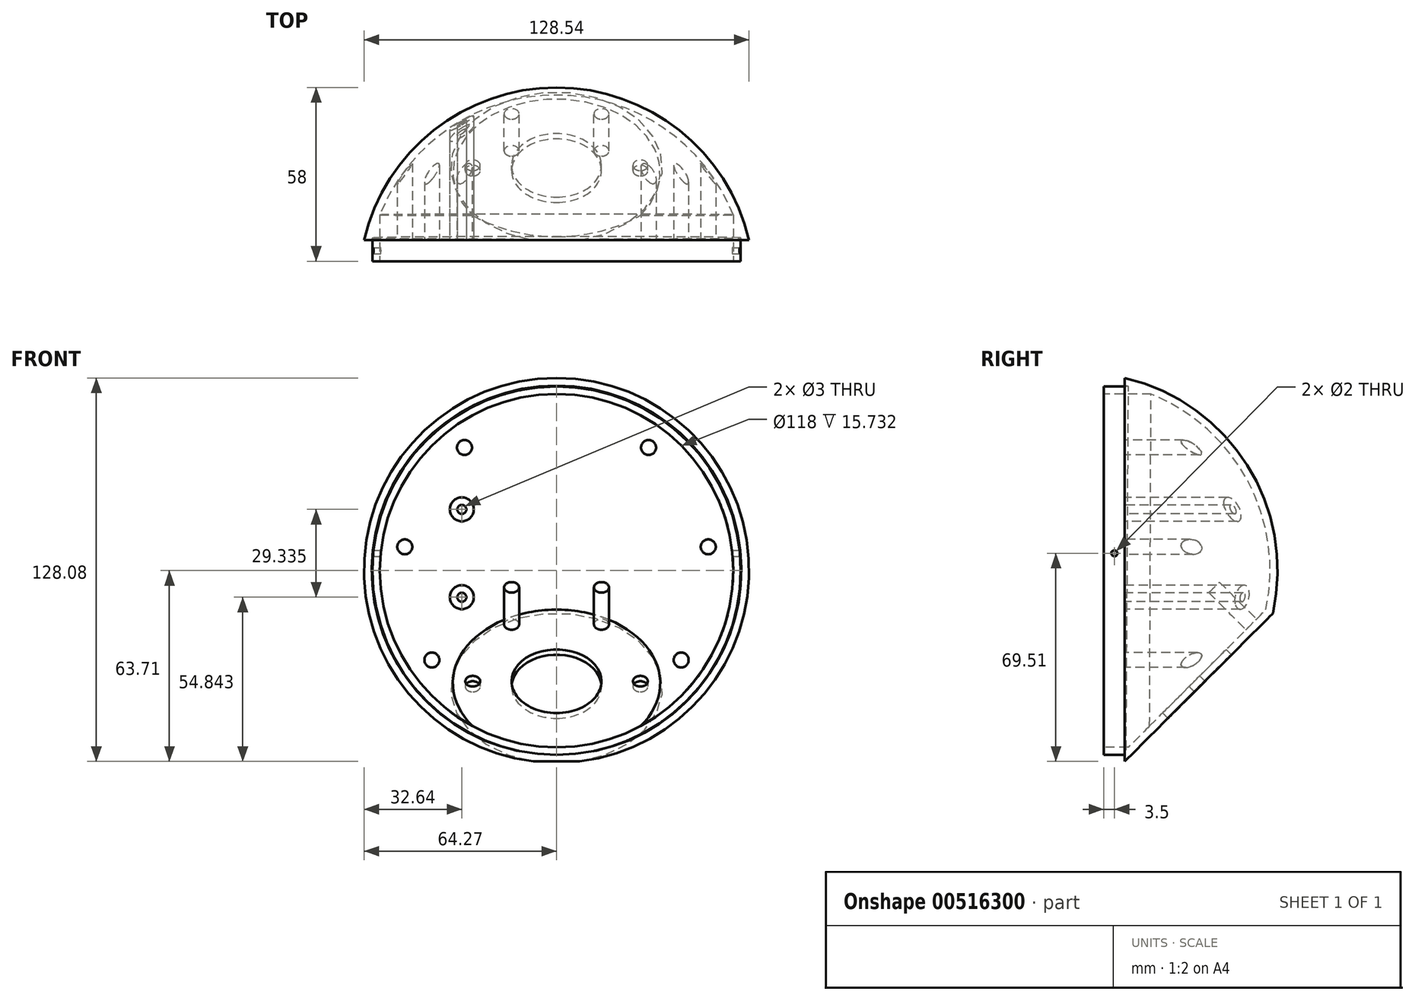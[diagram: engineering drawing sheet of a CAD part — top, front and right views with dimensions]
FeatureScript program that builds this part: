
annotation { "Feature Type Name" : "Feature", "Feature Type Description" : "" }
export const myFeature = defineFeature(function(context is Context, id is Id, definition is map)
    precondition{}
    {
        {
            var Q0;
            Q0=qCreatedBy(makeId("Front.planeOp"),FACE);
            var sketch = newSketch(context, id + "F0", { "sketchPlane" : qUnion([Q0])});
            skLineSegment(sketch, "E0", {"start": v(0, 60.3) * mm, "end": v(0, -71.7) * mm});
            skArc(sketch, "E1", {"start": v(0, 60.3) * mm, "mid": v(-66, -5.7) * mm, "end": v(0, -71.7) * mm});
            skSolve(sketch);
        }
        {
            var Q0;
            Q0=qSketchRegion(id+"F0",true);
            var Q1;
            Q1=sQuery(id+"F0.wireOp",EDGE,"E0");
            revolve(context, id + "F1", {"entities" : qUnion([Q0]), "axis" : qUnion([Q1]), "revolveType" : RevolveType.FULL});
        }
        {
            var Q0;
            Q0=qCreatedBy(makeId("Front.planeOp"),FACE);
            cPlane(context, id + "F2", {"entities" : qUnion([Q0]), "cplaneType" : CPlaneType.OFFSET, "offset" : 15 * mm, "oppositeDirection" : true, "width" : 150 * mm, "height" : 150 * mm});
        }
        {
            var Q0;
            Q0=qCreatedBy(id+"F2.planeOp",FACE);
            var sketch = newSketch(context, id + "F3", { "sketchPlane" : qUnion([Q0])});
            skLineSegment(sketch, "E2", {"start": v(74.9, -69.5) * mm, "end": v(-74.9, -69.5) * mm});
            skSolve(sketch);
        }
        {
            var Q0;
            Q0=sQuery(id+"F3.wireOp",EDGE,"E2");
            cPlane(context, id + "F4", {"entities" : qUnion([Q0]), "cplaneType" : CPlaneType.LINE_ANGLE, "offset" : 25 * mm, "angle" : 45 * degree, "width" : 150 * mm, "height" : 150 * mm});
        }
        {
            var Q0;
            Q0=qCreatedBy(id+"F4.planeOp",FACE);
            var sketch = newSketch(context, id + "F5", { "sketchPlane" : qUnion([Q0])});
            skLineSegment(sketch, "E3.bottom", {"start": v(55.31, 47.63) * mm, "end": v(-66.99, 47.63) * mm});
            skLineSegment(sketch, "E3.top", {"start": v(55.31, -55.11) * mm, "end": v(-66.99, -55.11) * mm});
            skLineSegment(sketch, "E3.left", {"start": v(55.31, 47.63) * mm, "end": v(55.31, -55.11) * mm});
            skLineSegment(sketch, "E3.right", {"start": v(-66.99, 47.63) * mm, "end": v(-66.99, -55.11) * mm});
            skSolve(sketch);
        }
        {
            var Q0;
            Q0=qSketchRegion(id+"F5",true);
            extrude(context, id + "F6", {"entities" : qUnion([Q0]), "operationType" : NewBodyOperationType.REMOVE, "oppositeDirection" : true, "depth" : 25 * mm, "offsetDistance" : 25 * mm});
        }
        {
            var Q0;
            Q0=qCreatedBy(id+"F2.planeOp",FACE);
            var sketch = newSketch(context, id + "F7", { "sketchPlane" : qUnion([Q0])});
            skLineSegment(sketch, "E4.bottom", {"start": v(74.83, 74.85) * mm, "end": v(-74.83, 74.85) * mm});
            skLineSegment(sketch, "E4.top", {"start": v(74.83, -74.85) * mm, "end": v(-74.83, -74.85) * mm});
            skLineSegment(sketch, "E4.left", {"start": v(74.83, 74.85) * mm, "end": v(74.83, -74.85) * mm});
            skLineSegment(sketch, "E4.right", {"start": v(-74.83, 74.85) * mm, "end": v(-74.83, -74.85) * mm});
            skPoint(sketch, "E4.middle", {"position": v(0, 0) * mm});
            skSolve(sketch);
        }
        {
            var Q0;
            Q0 = qSketchRegion(id + "F7", true);
            extrude(context, id + "F8", {"entities" : qUnion([Q0]), "operationType" : NewBodyOperationType.REMOVE, "depth" : 90 * mm, "offsetDistance" : 25 * mm});
        }
        {
            var Q0;
            Q0=makeQuery(id+"F8.boolean.opBoolean","COPY",FACE,{"derivedFrom":makeQuery(id+"F8.opExtrude","CAP_FACE",FACE,{"disambiguationData":[OSD([sQuery(id+"F7.wireOp",EDGE,"E4.bottom"),sQuery(id+"F7.wireOp",EDGE,"E4.top"),sQuery(id+"F7.wireOp",EDGE,"E4.left"),sQuery(id+"F7.wireOp",EDGE,"E4.right")])],"isStart":true})});
            shell(context, id + "F9", {"entities" : qUnion([Q0]), "thickness" : 2.5 * mm});
        }
        {
            var Q0;
            Q0=qCreatedBy(id+"F4.planeOp",FACE);
            var sketch = newSketch(context, id + "F10", { "sketchPlane" : qUnion([Q0])});
            skCircle(sketch, "E5", {"center": v(0, -3.19) * mm, "radius": 15 * mm});
            skCircle(sketch, "E6", {"center": v(-28, -3.19) * mm, "radius": 2.5 * mm});
            skCircle(sketch, "E7.MirrorC", {"center": v(28, -3.19) * mm, "radius": 2.5 * mm});
            skSolve(sketch);
        }
        {
            var Q0;
            Q0=qSketchRegion(id+"F10",true);
            extrude(context, id + "F11", {"entities" : qUnion([Q0]), "operationType" : NewBodyOperationType.REMOVE, "depth" : 5 * mm, "offsetDistance" : 25 * mm});
        }
        {
            var Q0;
            Q0=qCreatedBy(makeId("Front.planeOp"),FACE);
            cPlane(context, id + "F12", {"entities" : qUnion([Q0]), "cplaneType" : CPlaneType.OFFSET, "offset" : 8 * mm, "oppositeDirection" : true, "width" : 150 * mm, "height" : 150 * mm});
        }
        {
            var Q0;
            Q0=qCreatedBy(id+"F12.planeOp",FACE);
            var sketch = newSketch(context, id + "F13", { "sketchPlane" : qUnion([Q0])});
            skCircle(sketch, "E8", {"center": v(0, -5.8) * mm, "radius": 61.5 * mm});
            skCircle(sketch, "E9", {"center": v(0, -5.8) * mm, "radius": 59 * mm});
            skSolve(sketch);
        }
        {
            var Q0;
            Q0 = qSketchRegion(id + "F13", true);
            extrude(context, id + "F14", {"entities" : qUnion([Q0]), "operationType" : NewBodyOperationType.ADD, "endBound" : BoundingType.UP_TO_NEXT, "oppositeDirection" : true, "depth" : 25 * mm, "offsetDistance" : 25 * mm});
        }
        {
            var Q0;
            Q0=qCreatedBy(makeId("Right.planeOp"),FACE);
            cPlane(context, id + "F15", {"entities" : qUnion([Q0]), "cplaneType" : CPlaneType.OFFSET, "offset" : 75 * mm, "width" : 150 * mm, "height" : 150 * mm});
        }
        {
            var Q0;
            Q0=qCreatedBy(id+"F15.planeOp",FACE);
            var sketch = newSketch(context, id + "F16", { "sketchPlane" : qUnion([Q0])});
            skCircle(sketch, "E10", {"center": v(11.5, 0) * mm, "radius": 1 * mm});
            skSolve(sketch);
        }
        {
            var Q0;
            Q0 = qSketchRegion(id + "F16", true);
            extrude(context, id + "F17", {"entities" : qUnion([Q0]), "operationType" : NewBodyOperationType.REMOVE, "oppositeDirection" : true, "depth" : 150 * mm, "offsetDistance" : 25 * mm});
        }
        {
            var Q0;
            Q0=qCreatedBy(id+"F2.planeOp",FACE);
            var sketch = newSketch(context, id + "F18", { "sketchPlane" : qUnion([Q0])});
            skCircle(sketch, "E11", {"center": v(50.67, 2.15) * mm, "radius": 2.5 * mm});
            skCircle(sketch, "E12", {"center": v(30.74, 35.34) * mm, "radius": 2.5 * mm});
            skCircle(sketch, "E13.MirrorC", {"center": v(-30.74, 35.34) * mm, "radius": 2.5 * mm});
            skCircle(sketch, "E14.MirrorC", {"center": v(-50.67, 2.15) * mm, "radius": 2.5 * mm});
            skCircle(sketch, "E15", {"center": v(41.62, -35.65) * mm, "radius": 2.5 * mm});
            skCircle(sketch, "E16.MirrorC", {"center": v(-41.62, -35.65) * mm, "radius": 2.5 * mm});
            skCircle(sketch, "E17", {"center": v(-31.63, 14.67) * mm, "radius": 4 * mm});
            skCircle(sketch, "E18", {"center": v(-31.63, 14.67) * mm, "radius": 1.5 * mm});
            skCircle(sketch, "E19.MirrorC", {"center": v(-31.63, -14.67) * mm, "radius": 1.5 * mm});
            skCircle(sketch, "E20.MirrorC", {"center": v(-31.63, -14.67) * mm, "radius": 4 * mm});
            skSolve(sketch);
        }
        {
            var Q0;
            Q0 = qSketchRegion(id + "F18", true);
            extrude(context, id + "F19", {"entities" : qUnion([Q0]), "endBound" : BoundingType.UP_TO_NEXT, "oppositeDirection" : true, "depth" : 25 * mm, "offsetDistance" : 25 * mm});
        }
        {
            var Q0;
            Q0=qCreatedBy(id+"F4.planeOp",FACE);
            var sketch = newSketch(context, id + "F20", { "sketchPlane" : qUnion([Q0])});
            skCircle(sketch, "E21", {"center": v(15, 23.64) * mm, "radius": 2.5 * mm});
            skCircle(sketch, "E22.MirrorC", {"center": v(-15, 23.64) * mm, "radius": 2.5 * mm});
            skSolve(sketch);
        }
        {
            var Q0;
            Q0 = qSketchRegion(id + "F20", true);
            extrude(context, id + "F21", {"entities" : qUnion([Q0]), "operationType" : NewBodyOperationType.ADD, "depth" : 20 * mm, "offsetDistance" : 25 * mm});
        }
    });
